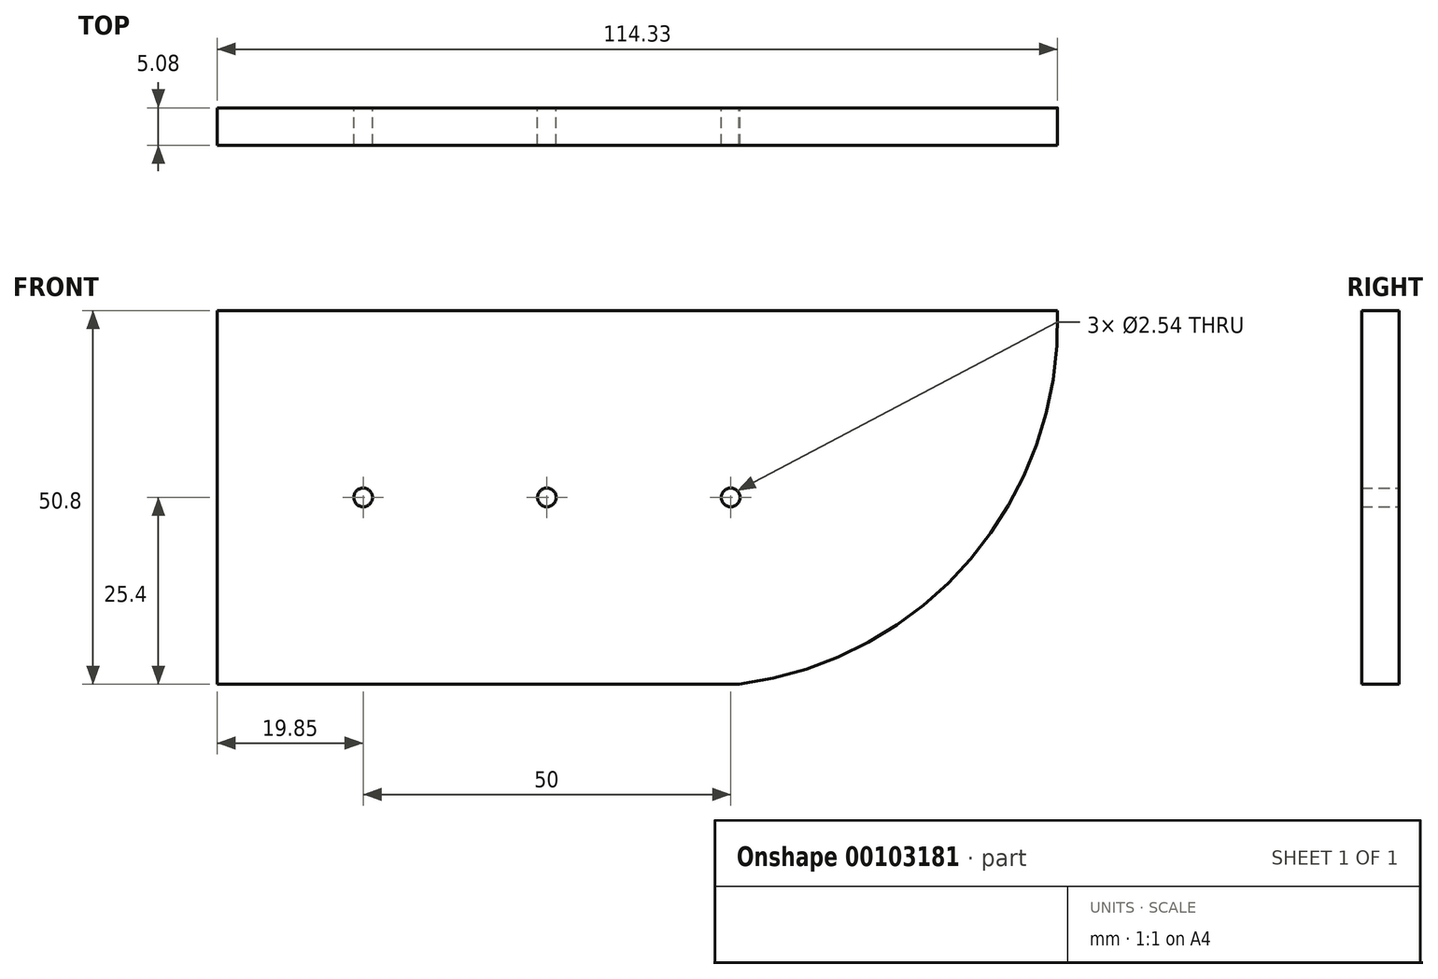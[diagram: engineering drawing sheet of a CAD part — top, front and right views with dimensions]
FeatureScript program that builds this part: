
annotation { "Feature Type Name" : "Feature", "Feature Type Description" : "" }
export const myFeature = defineFeature(function(context is Context, id is Id, definition is map)
    precondition{}
    {
        {
            var Q0;
            Q0=qCreatedBy(makeId("Front.planeOp"),FACE);
            var sketch = newSketch(context, id + "F0", { "sketchPlane" : qUnion([Q0])});
            skLineSegment(sketch, "E0.bottom", {"start": v(13.82, -25.4) * mm, "end": v(-57.15, -25.4) * mm});
            skLineSegment(sketch, "E0.top", {"start": v(57.15, 25.4) * mm, "end": v(-57.15, 25.4) * mm});
            skLineSegment(sketch, "E0.right", {"start": v(-57.15, -25.4) * mm, "end": v(-57.15, 25.4) * mm});
            skPoint(sketch, "E0.middle", {"position": v(0, 0) * mm});
            skArc(sketch, "E1", {"start": v(13.82, -25.4) * mm, "mid": v(45.33, -8.4) * mm, "end": v(57.15, 25.4) * mm});
            skPoint(sketch, "E2.orphan", {"position": v(57.15, -25.4) * mm});
            skCircle(sketch, "E3", {"center": v(-37.3, 0) * mm, "radius": 1.27 * mm});
            skCircle(sketch, "E4", {"center": v(-12.3, 0) * mm, "radius": 1.27 * mm});
            skCircle(sketch, "E5", {"center": v(12.7, 0) * mm, "radius": 1.27 * mm});
            skSolve(sketch);
        }
        {
            var Q0;
            Q0=makeQuery(id+"F0.imprint","IMPRINT",FACE,{"disambiguationData":[TD([[makeQuery(id+"F0.imprint","IMPRINT",EDGE,{"derivedFrom":sQuery(id+"F0.wireOp",EDGE,"E0.bottom")}),-1.0]])]});
            extrude(context, id + "F1", {"entities" : qUnion([Q0]), "depth" : 5.08 * mm});
        }
    });
